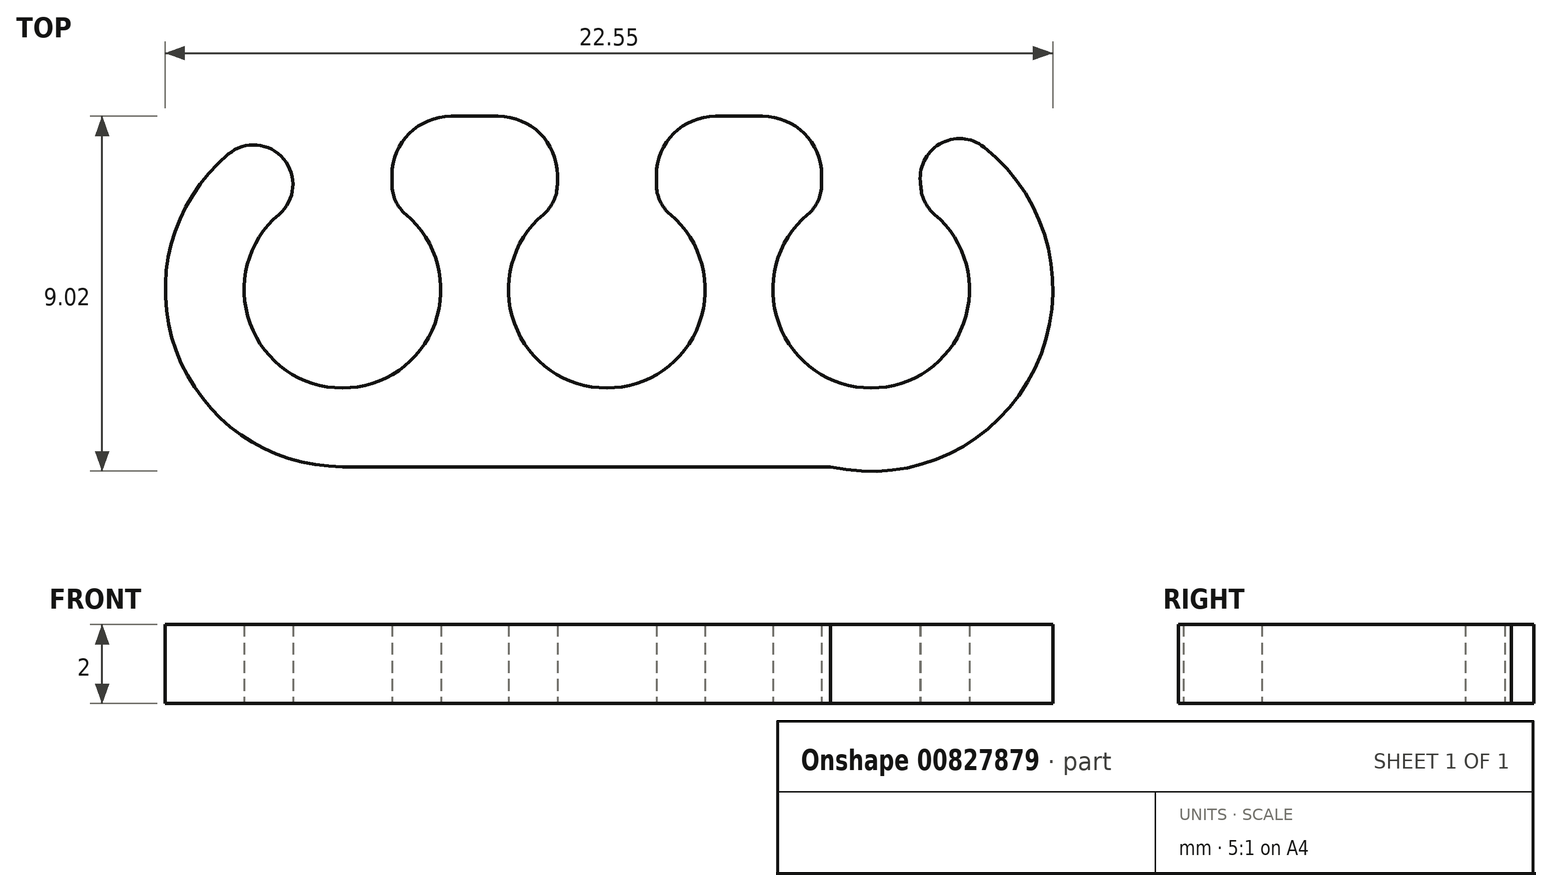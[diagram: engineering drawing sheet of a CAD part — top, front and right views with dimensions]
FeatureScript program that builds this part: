
annotation { "Feature Type Name" : "Feature", "Feature Type Description" : "" }
export const myFeature = defineFeature(function(context is Context, id is Id, definition is map)
    precondition{}
    {
        {
            var Q0;
            Q0=qCreatedBy(makeId("Top.planeOp"),FACE);
            var sketch = newSketch(context, id + "F0", { "sketchPlane" : qUnion([Q0])});
            skArc(sketch, "E0", {"start": v(-6.08, -9.53) * mm, "mid": v(-4.47, -13.94) * mm, "end": v(-2.85, -9.53) * mm});
            skArc(sketch, "E1.2.0.0", {"start": v(0.64, -9.53) * mm, "mid": v(2.25, -13.94) * mm, "end": v(3.86, -9.53) * mm});
            skArc(sketch, "E1.3.0.0", {"start": v(7.35, -9.53) * mm, "mid": v(8.97, -13.94) * mm, "end": v(10.58, -9.53) * mm});
            skArc(sketch, "E2", {"start": v(7.93, -15.94) * mm, "mid": v(13.13, -13.44) * mm, "end": v(11.83, -7.82) * mm});
            skArc(sketch, "E3", {"start": v(-7.37, -8) * mm, "mid": v(-8.7, -12.98) * mm, "end": v(-4.47, -15.94) * mm});
            skLineSegment(sketch, "E4.left", {"start": v(-3.2, -8.76) * mm, "end": v(-3.2, -8.53) * mm});
            skLineSegment(sketch, "E5.2.0.1", {"start": v(1, -8.76) * mm, "end": v(1, -8.53) * mm});
            skLineSegment(sketch, "E5.2.0.2", {"start": v(3.5, -8.76) * mm, "end": v(3.5, -8.53) * mm});
            skLineSegment(sketch, "E5.3.0.1", {"start": v(7.7, -8.76) * mm, "end": v(7.7, -8.53) * mm});
            skLineSegment(sketch, "E6.trimOffspring", {"start": v(5, -7.03) * mm, "end": v(6.2, -7.03) * mm});
            skArc(sketch, "E7.filletArc", {"start": v(-6.08, -9.53) * mm, "mid": v(-5.82, -9.18) * mm, "end": v(-5.72, -8.76) * mm});
            skArc(sketch, "E8.filletArc", {"start": v(-3.2, -8.76) * mm, "mid": v(-3.12, -9.18) * mm, "end": v(-2.85, -9.53) * mm});
            skArc(sketch, "E9.filletArc", {"start": v(-5.72, -8.76) * mm, "mid": v(-6.3, -7.86) * mm, "end": v(-7.37, -8) * mm});
            skArc(sketch, "E10.filletArc", {"start": v(3.5, -8.76) * mm, "mid": v(3.6, -9.18) * mm, "end": v(3.86, -9.53) * mm});
            skArc(sketch, "E11.filletArc", {"start": v(11.83, -7.82) * mm, "mid": v(10.7, -7.74) * mm, "end": v(10.22, -8.76) * mm});
            skArc(sketch, "E12.filletArc", {"start": v(10.22, -8.76) * mm, "mid": v(10.32, -9.18) * mm, "end": v(10.58, -9.53) * mm});
            skArc(sketch, "E13.filletArc", {"start": v(7.35, -9.53) * mm, "mid": v(7.61, -9.18) * mm, "end": v(7.7, -8.76) * mm});
            skArc(sketch, "E14.filletArc", {"start": v(0.64, -9.53) * mm, "mid": v(0.9, -9.18) * mm, "end": v(1, -8.76) * mm});
            skArc(sketch, "E15.filletArc", {"start": v(-1.7, -7.03) * mm, "mid": v(-2.77, -7.47) * mm, "end": v(-3.2, -8.53) * mm});
            skArc(sketch, "E16.filletArc", {"start": v(1, -8.53) * mm, "mid": v(0.55, -7.47) * mm, "end": v(-0.5, -7.03) * mm});
            skArc(sketch, "E17.filletArc", {"start": v(5, -7.03) * mm, "mid": v(3.95, -7.47) * mm, "end": v(3.5, -8.53) * mm});
            skArc(sketch, "E18.filletArc", {"start": v(7.7, -8.53) * mm, "mid": v(7.27, -7.47) * mm, "end": v(6.2, -7.03) * mm});
            skLineSegment(sketch, "E19.trimOffspring", {"start": v(-1.7, -7.03) * mm, "end": v(-0.5, -7.03) * mm});
            skLineSegment(sketch, "E20", {"start": v(-4.47, -15.94) * mm, "end": v(7.93, -15.94) * mm});
            skSolve(sketch);
        }
        {
            var Q0;
            Q0 = qSketchRegion(id + "F0", true);
            extrude(context, id + "F1", {"entities" : qUnion([Q0]), "depth" : 2 * mm, "offsetDistance" : 25 * mm});
        }
    });
